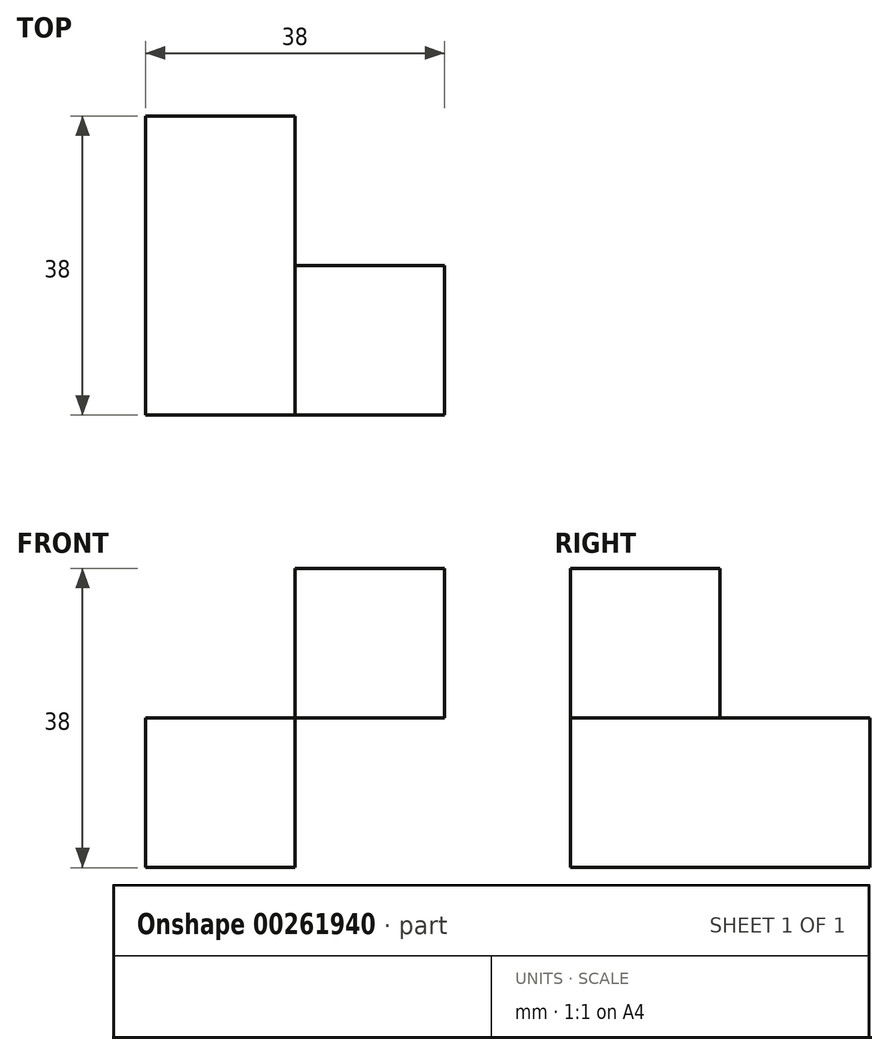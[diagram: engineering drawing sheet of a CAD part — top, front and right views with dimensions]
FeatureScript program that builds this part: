
annotation { "Feature Type Name" : "Feature", "Feature Type Description" : "" }
export const myFeature = defineFeature(function(context is Context, id is Id, definition is map)
    precondition{}
    {
        {
            var Q0;
            Q0=qCreatedBy(makeId("Front.planeOp"),FACE);
            var sketch = newSketch(context, id + "F0", { "sketchPlane" : qUnion([Q0])});
            skLineSegment(sketch, "E0.bottom", {"start": v(0, 0) * mm, "end": v(-19, 0) * mm});
            skLineSegment(sketch, "E0.top", {"start": v(0, -19) * mm, "end": v(-19, -19) * mm});
            skLineSegment(sketch, "E0.left", {"start": v(0, 0) * mm, "end": v(0, -19) * mm});
            skLineSegment(sketch, "E0.right", {"start": v(-19, 0) * mm, "end": v(-19, -19) * mm});
            skLineSegment(sketch, "E1.bottom", {"start": v(-19, 0) * mm, "end": v(0, 0) * mm});
            skLineSegment(sketch, "E1.top", {"start": v(-19, 19) * mm, "end": v(0, 19) * mm});
            skLineSegment(sketch, "E1.left", {"start": v(-19, 0) * mm, "end": v(-19, 19) * mm});
            skLineSegment(sketch, "E1.right", {"start": v(0, 0) * mm, "end": v(0, 19) * mm});
            skLineSegment(sketch, "E2.bottom", {"start": v(0, 19) * mm, "end": v(19, 19) * mm});
            skLineSegment(sketch, "E2.top", {"start": v(0, 0) * mm, "end": v(19, 0) * mm});
            skLineSegment(sketch, "E2.left", {"start": v(0, 19) * mm, "end": v(0, 0) * mm});
            skLineSegment(sketch, "E2.right", {"start": v(19, 19) * mm, "end": v(19, 0) * mm});
            skSolve(sketch);
        }
        {
            var Q0;
            Q0=makeQuery(id+"F0.imprint","IMPRINT",FACE,{"disambiguationData":[TD([[makeQuery(id+"F0.imprint","IMPRINT",EDGE,{"derivedFrom":sQuery(id+"F0.wireOp",EDGE,"E1.bottom")}),1.0]])]});
            var Q1;
            Q1=makeQuery(id+"F0.imprint","IMPRINT",FACE,{"disambiguationData":[TD([[makeQuery(id+"F0.imprint","IMPRINT",EDGE,{"derivedFrom":sQuery(id+"F0.wireOp",EDGE,"E0.top")}),-1.0]])]});
            extrude(context, id + "F1", {"entities" : qUnion([Q0, Q1]), "oppositeDirection" : true, "depth" : 38 * mm});
        }
        {
            var Q0;
            Q0=makeQuery(id+"F0.imprint","IMPRINT",FACE,{"disambiguationData":[TD([[makeQuery(id+"F0.imprint","IMPRINT",EDGE,{"derivedFrom":sQuery(id+"F0.wireOp",EDGE,"E2.bottom")}),-1.0]])]});
            extrude(context, id + "F2", {"entities" : qUnion([Q0]), "operationType" : NewBodyOperationType.ADD, "oppositeDirection" : true, "depth" : 19 * mm});
        }
    });
